# Revit family: 207_FLEXIT-ABC-VK-_ Zink
name_source: partatom
category: Air Terminals
revit_build: Autodesk Revit 2018 (Build: 20170223_1515(x64)
units: mm (PartAtom-declared; Revit-internal decimal feet)

## family parameters
Always vertical = Yes
Cut with Voids When Loaded = No
Part Type = Normal
Room Calculation Point = Yes
Round Connector Dimension = Use Diameter
Shared = No
Work Plane-Based = No

## types (4) — shared parameters
CAT0 = Yes
CL_Location_5000 = 5000 mm  [stored 16.4042 ft]
Description = Wall cowl V13 aluzinc
H1 = 2 mm  [stored 0.00656168 ft]
L_ARR = 400 mm  [stored 1.31234 ft]
Manufacturer = Flexit
QmdConnectorList = 201;D
URL = www.flexit.no
W_ARR = 400 mm  [stored 1.31234 ft]
magiPartTypeId = 207
magiProductFamilyId = FLEXIT-ABC-VK-* Zink
zero-valued in all types: CLBTZ, H_ARR

## per-type parameters (varying)
| type | AA | CC | D | L | Y1 | Y22 | Z1 | Z2 | Z3 | magiProductId |
| 125-115379 | 135 mm  [stored 0.442913 ft] | 123 mm | 125 mm | 105 mm  [stored 0.344488 ft] | 25 mm  [stored 0.082021 ft] | 196 mm  [stored 0.643045 ft] | 27 mm  [stored 0.0885827 ft] | 14 mm  [stored 0.0459318 ft] | 54 mm  [stored 0.177165 ft] | FLEXIT-ABC-VK-125 Zink |
| 160-115380 | 150 mm  [stored 0.492126 ft] | 150 mm  [stored 0.492126 ft] | 160 mm | 130 mm  [stored 0.426509 ft] | 30 mm  [stored 0.0984252 ft] | 240 mm  [stored 0.787402 ft] | 30 mm  [stored 0.0984252 ft] | 15 mm  [stored 0.0492126 ft] | 60 mm  [stored 0.19685 ft] | FLEXIT-ABC-VK-160 Zink |
| 200-115381 | 200 mm  [stored 0.656168 ft] | 173 mm | 200 mm | 140 mm  [stored 0.459318 ft] | 35 mm | 276 mm  [stored 0.905512 ft] | 40 mm  [stored 0.131234 ft] | 20 mm  [stored 0.0656168 ft] | 80 mm  [stored 0.262467 ft] | FLEXIT-ABC-VK-200 Zink |
| 250-115382 | 250 mm  [stored 0.82021 ft] | 223 mm | 250 mm | 190 mm  [stored 0.62336 ft] | 45 mm | 356 mm  [stored 1.16798 ft] | 50 mm  [stored 0.164042 ft] | 25 mm  [stored 0.082021 ft] | 100 mm  [stored 0.328084 ft] | FLEXIT-ABC-VK-250 Zink |

note: column(s) folded — value = type name in every type: MC Product Code

note: [stored X ft] marks values corroborated as IEEE doubles in the binary element streams (Revit-internal decimal feet)

## geometry (parser evidence)
native form markers: Sweep x2
no freeform markers — native parametric forms only
